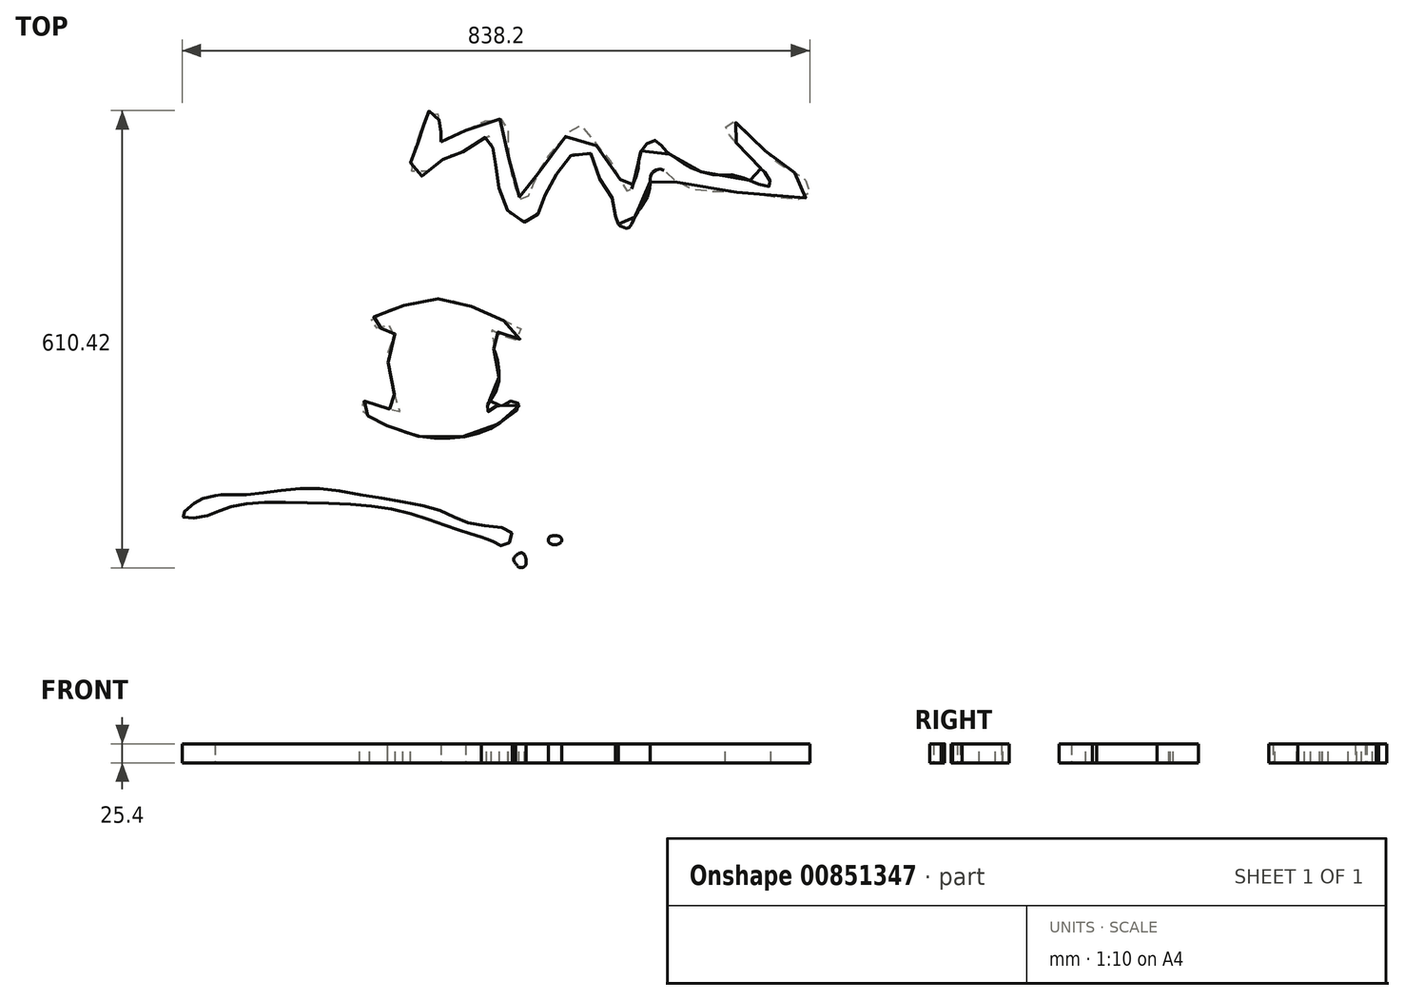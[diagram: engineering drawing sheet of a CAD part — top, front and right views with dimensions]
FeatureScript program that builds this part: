
annotation { "Feature Type Name" : "Feature", "Feature Type Description" : "" }
export const myFeature = defineFeature(function(context is Context, id is Id, definition is map)
    precondition{}
    {
        {
            var Q0;
            Q0=qCreatedBy(makeId("Top.planeOp"),FACE);
            var sketch = newSketch(context, id + "F0", { "sketchPlane" : qUnion([Q0])});
            skLineSegment(sketch, "E0", {"start": v(-243.2, 369.32) * mm, "end": v(-207.65, 334.53) * mm});
            skLineSegment(sketch, "E1", {"start": v(-207.65, 334.53) * mm, "end": v(-161.52, 342.75) * mm});
            skLineSegment(sketch, "E2", {"start": v(-100.75, -342.67) * mm, "end": v(-121.08, -338.6) * mm});
            skLineSegment(sketch, "E3", {"start": v(-121.08, -338.6) * mm, "end": v(-110.78, -354.33) * mm});
            skLineSegment(sketch, "E4", {"start": v(573.65, -473.95) * mm, "end": v(573.65, -473.95) * mm});
            skLineSegment(sketch, "E5", {"start": v(33, -361.7) * mm, "end": v(11.65, -377.97) * mm});
            skLineSegment(sketch, "E6", {"start": v(11.65, -377.97) * mm, "end": v(30.84, -396.59) * mm});
            skLineSegment(sketch, "E7", {"start": v(34.74, -390.35) * mm, "end": v(34.74, -390.35) * mm});
            skLineSegment(sketch, "E8", {"start": v(455.05, 111.04) * mm, "end": v(462.45, 93.18) * mm});
            skLineSegment(sketch, "E9", {"start": v(462.45, 93.18) * mm, "end": v(476.09, 109.03) * mm});
            skLineSegment(sketch, "E10", {"start": v(451.34, 368.52) * mm, "end": v(441.51, 400.57) * mm});
            skLineSegment(sketch, "E11", {"start": v(441.51, 400.57) * mm, "end": v(418.2, 397.44) * mm});
            skLineSegment(sketch, "E12", {"start": v(-476.82, 385.37) * mm, "end": v(-508.06, 389.07) * mm});
            skLineSegment(sketch, "E13", {"start": v(-508.06, 389.07) * mm, "end": v(-504.45, 350.45) * mm});
            skLineSegment(sketch, "E14", {"start": v(-457.16, 200.47) * mm, "end": v(-445.24, 183.73) * mm});
            skLineSegment(sketch, "E15", {"start": v(-445.24, 183.73) * mm, "end": v(-411.57, 215.68) * mm});
            skLineSegment(sketch, "E16", {"start": v(-291.39, -230.03) * mm, "end": v(-291.39, -230.03) * mm});
            skLineSegment(sketch, "E17", {"start": v(232.54, -104.44) * mm, "end": v(214.17, -94.94) * mm});
            skLineSegment(sketch, "E18", {"start": v(214.17, -94.94) * mm, "end": v(218.17, -116.28) * mm});
            skLineSegment(sketch, "E19", {"start": v(245.6, -201) * mm, "end": v(215.8, -211.71) * mm});
            skLineSegment(sketch, "E20", {"start": v(215.8, -211.71) * mm, "end": v(228.73, -225.46) * mm});
            skLineSegment(sketch, "E21", {"start": v(203.77, -230.8) * mm, "end": v(203.77, -230.8) * mm});
            skLineSegment(sketch, "E22", {"start": v(-219.89, 162.31) * mm, "end": v(-219.8, 149.22) * mm});
            skLineSegment(sketch, "E23", {"start": v(-219.8, 149.22) * mm, "end": v(-187, 164.24) * mm});
            skLineSegment(sketch, "E24", {"start": v(16.84, 39.18) * mm, "end": v(16.85, 39.18) * mm});
            skFitSpline(sketch, "E25", {"points": [v(573.65, -473.95) * mm, v(542.35, -455.59) * mm, v(477, -417.27) * mm, v(350.14, -409.44) * mm, v(248.86, -428.76) * mm, v(175.01, -446.44) * mm, v(139.76, -452.23) * mm, v(107.87, -453.72) * mm, v(75.62, -446.13) * mm, v(42.08, -431.72) * mm, v(15.47, -416.78) * mm, v(2.62, -402.25) * mm, v(-8.94, -400.14) * mm, v(-14.58, -416.13) * mm, v(-29.82, -430.98) * mm, v(-51.91, -449.2) * mm, v(-74.87, -460.76) * mm, v(-98.64, -463.8) * mm, v(-122.69, -465.91) * mm, v(-153.49, -466.73) * mm, v(-188.92, -466.54) * mm, v(-235.5, -453.54) * mm, v(-289.65, -432.48) * mm, v(-345.03, -410.2) * mm, v(-398.83, -396.97) * mm, v(-452.78, -395.56) * mm, v(-509.32, -394.08) * mm, v(-564.22, -401.07) * mm, v(-602.22, -414.17) * mm, v(-624.85, -424.55) * mm, v(-637.46, -427.05) * mm, v(-644.62, -420.6) * mm, v(-648.87, -411.22) * mm, v(-647.44, -396.15) * mm, v(-642.68, -372.36) * mm, v(-634.1, -340.98) * mm, v(-616.93, -305.5) * mm, v(-597.97, -279.83) * mm, v(-583.82, -260.15) * mm, v(-577.4, -251.96) * mm, v(-572.22, -238.97) * mm, v(-602.9, -256.96) * mm, v(-620.08, -264.43) * mm, v(-643.72, -281.68) * mm, v(-659.97, -293.94) * mm, v(-670.06, -300.63) * mm, v(-689.26, -304.48) * mm, v(-682.49, -251.33) * mm, v(-671.8, -211.59) * mm, v(-649.5, -164.63) * mm, v(-630.97, -136.12) * mm, v(-622.4, -120.96) * mm, v(-617.48, -105.25) * mm, v(-606.01, -87.77) * mm, v(-585.2, -65.72) * mm, v(-555.1, -36.51) * mm, v(-524.35, -8.98) * mm, v(-500.1, 19.31) * mm, v(-490.62, 50.8) * mm, v(-481.75, 79.8) * mm, v(-484.07, 112.15) * mm, v(-513.92, 139.48) * mm, v(-545.9, 187.15) * mm, v(-574.25, 259.89) * mm, v(-587.72, 324.05) * mm, v(-593.32, 371.37) * mm, v(-597.28, 396.82) * mm, v(-600.5, 420.25) * mm, v(-606.4, 439.89) * mm, v(-596.95, 459.66) * mm, v(-578.85, 467.66) * mm, v(-558.24, 476.23) * mm, v(-530.66, 478.8) * mm, v(-495.95, 479.4) * mm, v(-459.31, 479.67) * mm, v(-423.95, 474.23) * mm, v(-383.69, 458.92) * mm, v(-336.1, 438.11) * mm, v(-285.25, 407.33) * mm, v(-257.12, 381.9) * mm, v(-243.2, 369.32) * mm]});
            skFitSpline(sketch, "E26", {"points": [v(-161.52, 342.75) * mm, v(-149, 344.34) * mm, v(-118.9, 348.15) * mm, v(-68.22, 350.33) * mm, v(-5.25, 351.58) * mm, v(57.62, 350.73) * mm, v(119.17, 348.23) * mm, v(156.52, 335.78) * mm, v(184.35, 336.14) * mm, v(196.44, 350.23) * mm, v(213.53, 375.13) * mm, v(240.4, 409.68) * mm, v(277.72, 442.99) * mm, v(320.2, 473) * mm, v(377.43, 485.83) * mm, v(425.65, 487.9) * mm, v(476, 491.43) * mm, v(484.44, 459.94) * mm, v(494.35, 431) * mm, v(505.88, 386.65) * mm, v(517.81, 340.01) * mm, v(525.36, 292) * mm, v(526.45, 240.88) * mm, v(524.21, 186.37) * mm, v(512.86, 132.38) * mm, v(494.91, 95.77) * mm, v(476.12, 73.43) * mm, v(472.56, 49.8) * mm, v(477.78, 25.69) * mm, v(481.25, 0.37) * mm, v(490.87, -21.49) * mm, v(507.13, -38.77) * mm, v(527.22, -58.39) * mm, v(560.16, -81.5) * mm, v(606.15, -109.56) * mm, v(641.72, -136.9) * mm, v(677.43, -184.8) * mm, v(643.96, -191.38) * mm, v(623.21, -178.18) * mm, v(623.85, -199.48) * mm, v(640.61, -212.9) * mm, v(654.82, -239.12) * mm, v(666.04, -269.28) * mm, v(672.15, -297.77) * mm, v(673.22, -315.06) * mm, v(675.25, -326.1) * mm, v(668.88, -326.66) * mm, v(666.18, -322.43) * mm, v(663.69, -317.8) * mm, v(662.01, -299.26) * mm, v(652.69, -265.89) * mm, v(627.19, -224.38) * mm, v(604.24, -192.43) * mm, v(572.4, -179.41) * mm, v(581.01, -155.66) * mm, v(602.07, -160.93) * mm, v(617.97, -160.1) * mm, v(627.33, -160.4) * mm, v(638.96, -154.7) * mm, v(608.7, -137.43) * mm, v(591.91, -121.44) * mm, v(561.37, -105.19) * mm, v(537.84, -91.36) * mm, v(519.45, -77.65) * mm, v(497.7, -59.44) * mm, v(474.48, -34.4) * mm, v(457.6, 9.72) * mm, v(448.49, 71.95) * mm, v(419.27, 150) * mm, v(349.9, 222.71) * mm, v(267.18, 272.6) * mm, v(186.1, 309.97) * mm, v(103.92, 328.11) * mm, v(15.9, 332.03) * mm, v(-73.18, 334.01) * mm, v(-156.72, 323.89) * mm, v(-227.67, 303.08) * mm, v(-290.67, 279) * mm, v(-343.06, 248.47) * mm, v(-385.54, 213.29) * mm, v(-421.05, 176.06) * mm, v(-444.64, 131.23) * mm, v(-458.87, 78.91) * mm, v(-470.4, 27.27) * mm, v(-494, -16.84) * mm, v(-531.84, -46.34) * mm, v(-552.4, -64.23) * mm, v(-580.56, -87.06) * mm, v(-564.69, -90.37) * mm, v(-549.34, -93.7) * mm, v(-565.61, -115.83) * mm, v(-582.77, -125.9) * mm, v(-603.8, -142.28) * mm, v(-619.58, -157.8) * mm, v(-636.5, -179.18) * mm, v(-651.07, -209.91) * mm, v(-657.71, -233.69) * mm, v(-670.41, -263.88) * mm, v(-656.06, -263.77) * mm, v(-646.37, -258.5) * mm, v(-620.73, -243.67) * mm, v(-581.21, -224.82) * mm, v(-543.54, -211.61) * mm, v(-506.24, -215.55) * mm, v(-507.4, -229.77) * mm, v(-512.7, -235.62) * mm, v(-533.3, -244.13) * mm, v(-565.33, -271.17) * mm, v(-600.25, -321.38) * mm, v(-618.02, -357.8) * mm, v(-626.71, -393.51) * mm, v(-604, -394.64) * mm, v(-587.18, -385.26) * mm, v(-560.03, -379.8) * mm, v(-531.57, -375.79) * mm, v(-486.38, -371.7) * mm, v(-429.3, -371.73) * mm, v(-361.58, -383.35) * mm, v(-310.41, -403.04) * mm, v(-271.82, -420.23) * mm, v(-246.88, -430.07) * mm, v(-218.05, -441.5) * mm, v(-180.55, -447.6) * mm, v(-136.1, -448.02) * mm, v(-94.69, -445.05) * mm, v(-62.08, -428.37) * mm, v(-41.8, -411.13) * mm, v(-23.14, -387.54) * mm, v(-44.98, -367.27) * mm, v(-68.37, -353.02) * mm, v(-89.89, -346.14) * mm, v(-100.75, -342.67) * mm]});
            skFitSpline(sketch, "E27", {"points": [v(-110.78, -354.33) * mm, v(-103.85, -361.45) * mm, v(-94.7, -370.85) * mm, v(-109.11, -387.35) * mm, v(-154.46, -336.83) * mm, v(-245.32, -326.03) * mm, v(-375.33, -294.3) * mm, v(-482.24, -288.68) * mm, v(-530.28, -305.03) * mm, v(-552.78, -295.9) * mm, v(-508.82, -274.82) * mm, v(-460.29, -277.92) * mm, v(-367.93, -277.49) * mm, v(-278.42, -301.23) * mm, v(-235.7, -307.2) * mm, v(-190.4, -327.32) * mm, v(-199.03, -303.19) * mm, v(-235.97, -296.82) * mm, v(-281.66, -274.64) * mm, v(-330.67, -261.92) * mm, v(-370.1, -255.42) * mm, v(-398, -252.17) * mm, v(-425.08, -251.13) * mm, v(-445.1, -250.5) * mm, v(-460.75, -250.15) * mm, v(-465.98, -241.1) * mm, v(-457.74, -231.16) * mm, v(-433.34, -235.12) * mm, v(-393.22, -233.61) * mm, v(-336.56, -239.1) * mm, v(-270.03, -258.8) * mm, v(-218.2, -282.7) * mm, v(-176.71, -303.93) * mm, v(-159.37, -309.21) * mm, v(-145.6, -318.27) * mm, v(-141.98, -308.04) * mm, v(-135.66, -299.3) * mm, v(-118.7, -266.65) * mm, v(-77.86, -223.5) * mm, v(4.1, -210.8) * mm, v(58.98, -240.42) * mm, v(88.01, -270.75) * mm, v(101.08, -287.62) * mm, v(111.64, -304.39) * mm, v(114.3, -318.63) * mm, v(125.02, -327.51) * mm, v(138.05, -316.2) * mm, v(161.56, -308.28) * mm, v(201.54, -293.4) * mm, v(258.8, -274.96) * mm, v(343.2, -257.85) * mm, v(385.9, -255.48) * mm, v(475.6, -244.27) * mm, v(459.64, -259) * mm, v(448.93, -259.6) * mm, v(427.87, -261.91) * mm, v(397.36, -262.66) * mm, v(355.05, -270) * mm, v(304.97, -281.6) * mm, v(249.34, -293.8) * mm, v(206.15, -312.54) * mm, v(175.33, -314.96) * mm, v(166.4, -332.54) * mm, v(201.25, -321.46) * mm, v(232.2, -319.97) * mm, v(302.83, -310.06) * mm, v(371.72, -310.4) * mm, v(431.7, -313.17) * mm, v(471.17, -324.1) * mm, v(491.72, -327.43) * mm, v(501.74, -336.1) * mm, v(499.3, -340.52) * mm, v(496.8, -342.3) * mm, v(480.54, -340.12) * mm, v(450.15, -329.95) * mm, v(400.9, -325.43) * mm, v(344.44, -320.84) * mm, v(276.03, -328.4) * mm, v(232.77, -334.44) * mm, v(152.72, -353.5) * mm, v(218.34, -359.44) * mm, v(257.79, -361.43) * mm, v(316.35, -358.22) * mm, v(369.4, -364.1) * mm, v(416, -374.3) * mm, v(462.61, -389.67) * mm, v(506.6, -422.15) * mm, v(545.35, -432.4) * mm, v(594.36, -467.44) * mm, v(596.55, -434.47) * mm, v(590.26, -410.98) * mm, v(581.8, -379.93) * mm, v(564.2, -353.73) * mm, v(546.3, -333.53) * mm, v(531.05, -324.35) * mm, v(522.2, -321.74) * mm, v(520.45, -318.1) * mm, v(518.21, -306.85) * mm, v(556.62, -301.5) * mm, v(591.08, -316.16) * mm, v(630.31, -334.42) * mm, v(650.88, -350.43) * mm, v(661.16, -355.33) * mm, v(667.49, -352.1) * mm, v(672.36, -347.5) * mm, v(678.27, -353.28) * mm, v(682.68, -366.5) * mm, v(687.56, -381.62) * mm, v(685.13, -408.49) * mm, v(669.52, -400.31) * mm, v(663.62, -391.15) * mm, v(655.63, -382.02) * mm, v(644.88, -367.72) * mm, v(628.32, -352) * mm, v(605.53, -339.85) * mm, v(589.63, -333.58) * mm, v(575.71, -335.44) * mm, v(579.45, -347.06) * mm, v(591.97, -369.16) * mm, v(606.16, -415.35) * mm, v(617.68, -452.57) * mm, v(608.16, -493.19) * mm, v(593.59, -486.53) * mm, v(584.51, -481.5) * mm, v(577.48, -476.61) * mm, v(573.65, -473.95) * mm]});
            skFitSpline(sketch, "E28", {"points": [v(205.22, -418.08) * mm, v(221.1, -414.75) * mm, v(253.53, -407.96) * mm, v(300.27, -400.59) * mm, v(340.99, -396.5) * mm, v(373.76, -393.93) * mm, v(392.38, -392.63) * mm, v(417.36, -385.83) * mm, v(350.37, -376.76) * mm, v(315.37, -374.99) * mm, v(249.88, -372.75) * mm, v(200.55, -376.43) * mm, v(163.55, -380.2) * mm, v(123.98, -386.25) * mm, v(101.98, -391.43) * mm, v(66.75, -393.14) * mm, v(79.33, -380.28) * mm, v(85.76, -374.23) * mm, v(89.98, -366.32) * mm, v(91.89, -358) * mm, v(93.56, -348.78) * mm, v(84.59, -343.02) * mm, v(73.64, -344.45) * mm, v(60.07, -346.87) * mm, v(46.2, -352.9) * mm, v(37.4, -358.76) * mm, v(33, -361.7) * mm]});
            skFitSpline(sketch, "E29", {"points": [v(30.84, -396.59) * mm, v(34.27, -399.59) * mm, v(39.67, -404.31) * mm, v(47.85, -411.17) * mm, v(54.81, -406.88) * mm, v(58.3, -398.27) * mm, v(70.8, -402.8) * mm, v(73.43, -413.22) * mm, v(76.98, -426.23) * mm, v(97.65, -430.8) * mm, v(116.24, -437.27) * mm, v(141.18, -432.02) * mm, v(168.67, -426.48) * mm, v(191.9, -421.14) * mm, v(205.22, -418.08) * mm]});
            skFitSpline(sketch, "E30", {"points": [v(34.74, -390.35) * mm, v(32.87, -388) * mm, v(29.02, -383.13) * mm, v(37.66, -373.41) * mm, v(50.5, -368.1) * mm, v(60.54, -361.05) * mm, v(73.52, -358.6) * mm, v(72.66, -366.91) * mm, v(71.86, -372) * mm, v(68.61, -375.68) * mm, v(64.05, -376.45) * mm, v(59.27, -377.33) * mm, v(55.04, -380.7) * mm, v(51.92, -386.2) * mm, v(49.08, -392.74) * mm, v(40.74, -395.23) * mm, v(36.85, -392.07) * mm, v(34.74, -390.35) * mm]});
            skFitSpline(sketch, "E31", {"points": [v(497.38, 150.14) * mm, v(498.87, 157.77) * mm, v(502.63, 177.01) * mm, v(504.1, 211.5) * mm, v(504.6, 256.2) * mm, v(503.94, 302.97) * mm, v(497.98, 350.82) * mm, v(486.66, 390.3) * mm, v(477.48, 425.94) * mm, v(468.9, 446.15) * mm, v(466.68, 464.08) * mm, v(451.7, 463.92) * mm, v(434.87, 465.62) * mm, v(401.51, 465.77) * mm, v(360.12, 464.63) * mm, v(312.25, 446) * mm, v(276.7, 416.02) * mm, v(243.72, 382.05) * mm, v(227.93, 354.81) * mm, v(204.85, 332.43) * mm, v(213.02, 322.82) * mm, v(219.5, 319.37) * mm, v(229.05, 314.98) * mm, v(240.57, 309.53) * mm, v(255.94, 315.73) * mm, v(278.93, 340.45) * mm, v(318.46, 371.88) * mm, v(370.78, 402.77) * mm, v(412.28, 419.77) * mm, v(446.95, 420.52) * mm, v(465.14, 398) * mm, v(476.1, 353.09) * mm, v(484.44, 289.36) * mm, v(481.26, 215.81) * mm, v(467.25, 165.1) * mm, v(452.15, 138.2) * mm, v(450.03, 123.37) * mm, v(453.3, 115.32) * mm, v(455.05, 111.04) * mm]});
            skFitSpline(sketch, "E32", {"points": [v(476.09, 109.03) * mm, v(478.82, 112.78) * mm, v(484.82, 121.03) * mm, v(491.88, 134.92) * mm, v(495.57, 145.14) * mm, v(497.38, 150.14) * mm]});
            skFitSpline(sketch, "E33", {"points": [v(-462.14, 145.82) * mm, v(-462.2, 148.81) * mm, v(-462.38, 156.93) * mm, v(-468.04, 170.41) * mm, v(-481.17, 195.91) * mm, v(-498.96, 237.46) * mm, v(-516.34, 294.59) * mm, v(-525.84, 345.89) * mm, v(-535.43, 398.78) * mm, v(-484.97, 417.77) * mm, v(-441.29, 396.88) * mm, v(-392.38, 379.6) * mm, v(-350.92, 354.59) * mm, v(-321.57, 330.01) * mm, v(-301.18, 313.02) * mm, v(-290.12, 306.26) * mm, v(-280.33, 306.17) * mm, v(-272.54, 310.17) * mm, v(-263.68, 313.25) * mm, v(-254.45, 316.53) * mm, v(-246.27, 320.1) * mm, v(-240.6, 323.5) * mm, v(-236.3, 328.8) * mm, v(-242.5, 336.12) * mm, v(-248.7, 345.5) * mm, v(-263.64, 362.63) * mm, v(-276.86, 374.91) * mm, v(-286.43, 382.75) * mm]});
            skFitSpline(sketch, "E34", {"points": [v(-286.43, 382.75) * mm, v(-298.82, 392.9) * mm, v(-336.76, 419.1) * mm, v(-404.53, 449.53) * mm, v(-475.24, 462.74) * mm, v(-528.2, 457.6) * mm, v(-557.42, 452.61) * mm, v(-590.15, 441.25) * mm, v(-571.32, 388.84) * mm, v(-569.35, 336.97) * mm, v(-554.78, 274.77) * mm, v(-538.6, 226.2) * mm, v(-520.38, 187.91) * mm, v(-497.37, 161.3) * mm, v(-483.12, 144.87) * mm, v(-466.84, 134.75) * mm, v(-463.68, 142.2) * mm, v(-462.14, 145.82) * mm]});
            skFitSpline(sketch, "E35", {"points": [v(455.98, 187.73) * mm, v(459.2, 204.97) * mm, v(466.6, 244.55) * mm, v(464.2, 305.92) * mm, v(455.49, 348.33) * mm, v(451.34, 368.52) * mm]});
            skFitSpline(sketch, "E36", {"points": [v(418.2, 397.44) * mm, v(413.1, 396.45) * mm, v(401.97, 394.29) * mm, v(385.68, 388.85) * mm, v(360.93, 378.95) * mm, v(327.13, 354.25) * mm, v(304.32, 328.44) * mm, v(261.68, 304.06) * mm, v(277.18, 291.09) * mm, v(289.34, 283.14) * mm, v(316.31, 267.33) * mm, v(352.03, 243.5) * mm, v(390.27, 210.88) * mm, v(413.34, 183.24) * mm, v(425.57, 165.12) * mm, v(431.62, 158.55) * mm, v(439.49, 154.58) * mm, v(444.84, 163.53) * mm, v(450.41, 173.22) * mm, v(453.98, 182.53) * mm, v(455.98, 187.73) * mm]});
            skFitSpline(sketch, "E37", {"points": [v(-348.06, 267.66) * mm, v(-342.86, 271.01) * mm, v(-333.8, 276.85) * mm, v(-324.36, 284.5) * mm, v(-314.48, 288.7) * mm, v(-318.44, 302.77) * mm, v(-332.7, 314.67) * mm, v(-358.04, 336.5) * mm, v(-393.78, 357.74) * mm, v(-435.23, 377.23) * mm, v(-463.56, 382.78) * mm, v(-476.82, 385.37) * mm]});
            skFitSpline(sketch, "E38", {"points": [v(-504.45, 350.45) * mm, v(-501.4, 332.71) * mm, v(-494.98, 295.37) * mm, v(-479.68, 244.6) * mm, v(-463.9, 213.67) * mm, v(-457.16, 200.47) * mm]});
            skFitSpline(sketch, "E39", {"points": [v(-411.57, 215.68) * mm, v(-404.6, 222.01) * mm, v(-390.36, 234.96) * mm, v(-369.22, 252.38) * mm, v(-354.66, 262.9) * mm, v(-348.06, 267.66) * mm]});
            skFitSpline(sketch, "E40", {"points": [v(-120.2, -414.38) * mm, v(-121.1, -412.44) * mm, v(-123, -408.37) * mm, v(-118.87, -402.32) * mm, v(-113.36, -399.46) * mm, v(-109.05, -401.26) * mm, v(-107.94, -403.02) * mm, v(-107.53, -403.93) * mm]});
            skFitSpline(sketch, "E41", {"points": [v(-107.53, -403.93) * mm, v(-107.42, -404.2) * mm, v(-106.75, -405.91) * mm, v(-106.13, -410.01) * mm, v(-107.13, -416.5) * mm, v(-114.65, -419.2) * mm, v(-118.17, -416.15) * mm, v(-120.2, -414.38) * mm]});
            skFitSpline(sketch, "E42", {"points": [v(-166.1, -378.3) * mm, v(-202.86, -366.75) * mm, v(-281.14, -342.14) * mm, v(-396.32, -332.45) * mm, v(-494.53, -336.35) * mm, v(-535.9, -350.7) * mm, v(-565.38, -350.1) * mm, v(-545.46, -330.7) * mm, v(-531.35, -325.12) * mm, v(-521.57, -323.24) * mm]});
            skFitSpline(sketch, "E43", {"points": [v(-521.57, -323.24) * mm, v(-512.63, -321.52) * mm, v(-475.39, -321.43) * mm, v(-401.55, -313.3) * mm, v(-310.84, -324.56) * mm, v(-222.18, -342.64) * mm, v(-174.37, -361.45) * mm, v(-125.77, -372.06) * mm, v(-133.77, -389.85) * mm, v(-149.72, -384.81) * mm, v(-159.56, -380.9) * mm, v(-166.1, -378.3) * mm]});
            skFitSpline(sketch, "E44", {"points": [v(-76.62, -382.4) * mm, v(-76.32, -381.32) * mm, v(-75.67, -378.95) * mm, v(-71.97, -376.92) * mm, v(-67.69, -376.17) * mm, v(-63.3, -376.92) * mm, v(-59.84, -378.95) * mm, v(-58.72, -381.32) * mm, v(-58.72, -382.4) * mm]});
            skFitSpline(sketch, "E45", {"points": [v(-58.72, -382.4) * mm, v(-58.72, -382.4) * mm, v(-58.72, -383.48) * mm, v(-59.84, -385.84) * mm, v(-63.3, -387.88) * mm, v(-67.69, -388.63) * mm, v(-71.97, -387.88) * mm, v(-75.67, -385.84) * mm, v(-76.32, -383.48) * mm, v(-76.62, -382.4) * mm]});
            skFitSpline(sketch, "E46", {"points": [v(-291.39, -230.03) * mm, v(-297.15, -227.38) * mm, v(-307.46, -222.63) * mm, v(-319.64, -214.68) * mm, v(-326.46, -207.58) * mm, v(-327.79, -199.88) * mm, v(-321.17, -197.05) * mm, v(-306.62, -202.72) * mm, v(-294.65, -205.6) * mm, v(-271.28, -210.34) * mm, v(-280.92, -190.12) * mm, v(-286.1, -172.66) * mm, v(-290.5, -144.33) * mm, v(-288.6, -121.16) * mm, v(-281.46, -107.26) * mm, v(-284.68, -94.27) * mm, v(-294.24, -99.12) * mm, v(-301.59, -99.63) * mm, v(-307.72, -99.4) * mm, v(-315.21, -95.27) * mm, v(-304, -79.9) * mm, v(-283.8, -73.75) * mm, v(-256.97, -65.03) * mm, v(-231.48, -60.36) * mm, v(-208.18, -61.68) * mm, v(-181.8, -69.62) * mm, v(-150.68, -81.04) * mm, v(-130.1, -92.37) * mm, v(-107.97, -106.2) * mm, v(-119.32, -115.61) * mm, v(-130.62, -112.87) * mm, v(-139.4, -108.9) * mm, v(-150.46, -98.23) * mm, v(-150.97, -119.6) * mm, v(-146.53, -134.04) * mm, v(-142.36, -155.66) * mm, v(-143.37, -173.68) * mm, v(-149.72, -189.57) * mm, v(-156.48, -198.57) * mm, v(-157.8, -210.83) * mm, v(-144.51, -203.07) * mm, v(-135.67, -201.97) * mm, v(-123.45, -196.37) * mm, v(-115.44, -203.66) * mm, v(-126.98, -215.42) * mm, v(-140.48, -225.35) * mm, v(-166.74, -239) * mm, v(-203.35, -245.74) * mm, v(-247.82, -244.13) * mm, v(-276.9, -234.71) * mm, v(-291.39, -230.03) * mm]});
            skFitSpline(sketch, "E47", {"points": [v(203.77, -230.8) * mm, v(199.56, -229.08) * mm, v(189.28, -224.9) * mm, v(171.47, -220.35) * mm, v(144.96, -215.2) * mm, v(113.39, -208.44) * mm, v(87.2, -196.73) * mm, v(67.64, -186.74) * mm, v(67.67, -176.92) * mm, v(71.62, -173.97) * mm, v(77.18, -173.75) * mm, v(86.35, -171.25) * mm, v(86.87, -152.84) * mm, v(87.92, -132.92) * mm, v(86.59, -111.37) * mm, v(86.58, -95.72) * mm, v(80.47, -89.86) * mm, v(75.32, -89.19) * mm, v(73.31, -84.57) * mm, v(73.12, -78.5) * mm, v(79.23, -70.85) * mm, v(93.09, -66.12) * mm, v(112.51, -61.51) * mm, v(134.56, -57.35) * mm, v(157.86, -57.94) * mm, v(185.64, -65.4) * mm, v(216.6, -75.67) * mm, v(242.95, -88.92) * mm, v(258.49, -100.64) * mm, v(257.5, -114.3) * mm, v(244.2, -111.43) * mm, v(237.43, -107.37) * mm, v(232.54, -104.44) * mm]});
            skFitSpline(sketch, "E48", {"points": [v(218.17, -116.28) * mm, v(218.67, -120.98) * mm, v(219.75, -131.16) * mm, v(218.7, -146.65) * mm, v(215.96, -161.3) * mm, v(212.52, -174.15) * mm, v(211.4, -182.23) * mm, v(210.51, -190.92) * mm, v(220.36, -188.18) * mm, v(229.93, -185.9) * mm, v(247.7, -179.28) * mm, v(261.84, -174.2) * mm, v(282.16, -172.13) * mm, v(280.17, -185.52) * mm, v(271.08, -190) * mm, v(260.17, -195.58) * mm, v(250.82, -199.05) * mm, v(245.6, -201) * mm]});
            skFitSpline(sketch, "E49", {"points": [v(228.73, -225.46) * mm, v(232.05, -227.92) * mm, v(236.36, -231.1) * mm, v(238.4, -240.53) * mm, v(229.1, -238.66) * mm, v(221.93, -238) * mm, v(212.69, -234.98) * mm, v(206.75, -232.2) * mm, v(203.77, -230.8) * mm]});
            skFitSpline(sketch, "E50", {"points": [v(16.85, 39.18) * mm, v(16.11, 40.4) * mm, v(14.33, 43.34) * mm, v(13.16, 49.04) * mm, v(12.84, 62.07) * mm, v(2.86, 84.86) * mm, v(-11.57, 107.25) * mm, v(-24.69, 139.09) * mm, v(-51.1, 126.8) * mm, v(-66.47, 104.83) * mm, v(-80.73, 79.2) * mm, v(-87.95, 58.11) * mm, v(-96.1, 45.86) * mm, v(-110.66, 42.38) * mm, v(-128.69, 54.39) * mm, v(-140.75, 81.21) * mm, v(-145.8, 108.67) * mm, v(-148.43, 131.7) * mm, v(-150.72, 143.13) * mm, v(-155.2, 156.9) * mm, v(-179.55, 140.73) * mm, v(-204.55, 132.27) * mm, v(-227.75, 117.83) * mm, v(-253.38, 102.15) * mm, v(-259.78, 127.74) * mm, v(-251.42, 145.63) * mm, v(-245.52, 166.94) * mm, v(-239.84, 178.54) * mm, v(-237.06, 189.89) * mm, v(-225.92, 188.4) * mm, v(-221.87, 176.23) * mm, v(-220.6, 167.33) * mm, v(-219.89, 162.31) * mm]});
            skFitSpline(sketch, "E51", {"points": [v(-187, 164.24) * mm, v(-177.19, 169.18) * mm, v(-162.4, 176.64) * mm, v(-135.05, 177.3) * mm, v(-130.05, 149.02) * mm, v(-128.94, 124.13) * mm, v(-123.6, 96.75) * mm, v(-118.57, 82.27) * mm, v(-109.17, 71.28) * mm, v(-98.48, 86.76) * mm, v(-90.73, 105.56) * mm, v(-73.5, 133.6) * mm, v(-56.32, 153.45) * mm, v(-34.67, 171.91) * mm, v(-16.17, 149.92) * mm, v(0.8, 130.83) * mm, v(14.48, 109.19) * mm, v(22.33, 93.4) * mm, v(26.35, 87.28) * mm, v(31.69, 81.15) * mm, v(35.82, 90) * mm, v(38.96, 98.76) * mm, v(44.19, 117.1) * mm, v(46.8, 136.07) * mm, v(65.42, 151.27) * mm, v(78.84, 139.12) * mm, v(89.61, 130.36) * mm, v(100.19, 123.34) * mm, v(117.65, 112.92) * mm, v(150.62, 104.78) * mm, v(176.2, 103.81) * mm, v(219.8, 90.21) * mm, v(213.8, 107.1) * mm, v(204.41, 116.27) * mm, v(191.58, 130.1) * mm, v(177.2, 143.78) * mm, v(168.32, 155.49) * mm, v(159.7, 165.08) * mm, v(169, 176.9) * mm, v(186.43, 160.87) * mm, v(201.42, 148.11) * mm, v(219.24, 130.77) * mm, v(234.6, 118.64) * mm, v(248.83, 109.9) * mm, v(259.96, 104.22) * mm, v(267.34, 97.75) * mm, v(270.9, 76.7) * mm, v(205.29, 78.57) * mm, v(156.15, 82.46) * mm, v(100.76, 91.75) * mm, v(74.44, 112.88) * mm, v(60.52, 105.42) * mm, v(59.08, 87.33) * mm, v(50.07, 66.47) * mm, v(39.41, 49.8) * mm, v(29.9, 34.1) * mm, v(22.6, 35.7) * mm, v(19.5, 37) * mm, v(17.71, 38.47) * mm, v(16.84, 39.18) * mm]});
            skSolve(sketch);
        }
        {
            var Q0;
            Q0=makeQuery(id+"F0.imprint","IMPRINT",FACE,{"disambiguationData":[TD([[makeQuery(id+"F0.imprint","IMPRINT",EDGE,{"derivedFrom":sQuery(id+"F0.wireOp",EDGE,"E16")}),-1.0]])]});
            var Q1;
            Q1=makeQuery(id+"F0.imprint","IMPRINT",FACE,{"disambiguationData":[TD([[makeQuery(id+"F0.imprint","IMPRINT",EDGE,{"derivedFrom":sQuery(id+"F0.wireOp",EDGE,"E22")}),-1.0]])]});
            var Q2;
            Q2=makeQuery(id+"F0.imprint","IMPRINT",FACE,{"disambiguationData":[TD([[makeQuery(id+"F0.imprint","IMPRINT",EDGE,{"derivedFrom":sQuery(id+"F0.wireOp",EDGE,"E40")}),-1.0]])]});
            var Q3;
            Q3=makeQuery(id+"F0.imprint","IMPRINT",FACE,{"disambiguationData":[TD([[makeQuery(id+"F0.imprint","IMPRINT",EDGE,{"derivedFrom":sQuery(id+"F0.wireOp",EDGE,"E42")}),-1.0]])]});
            var Q4;
            Q4=makeQuery(id+"F0.imprint","IMPRINT",FACE,{"disambiguationData":[TD([[makeQuery(id+"F0.imprint","IMPRINT",EDGE,{"derivedFrom":sQuery(id+"F0.wireOp",EDGE,"E44")}),-1.0]])]});
            extrude(context, id + "F1", {"entities" : qUnion([Q0, Q1, Q2, Q3, Q4]), "depth" : 25.4 * mm, "offsetDistance" : 25.4 * mm});
        }
    });
